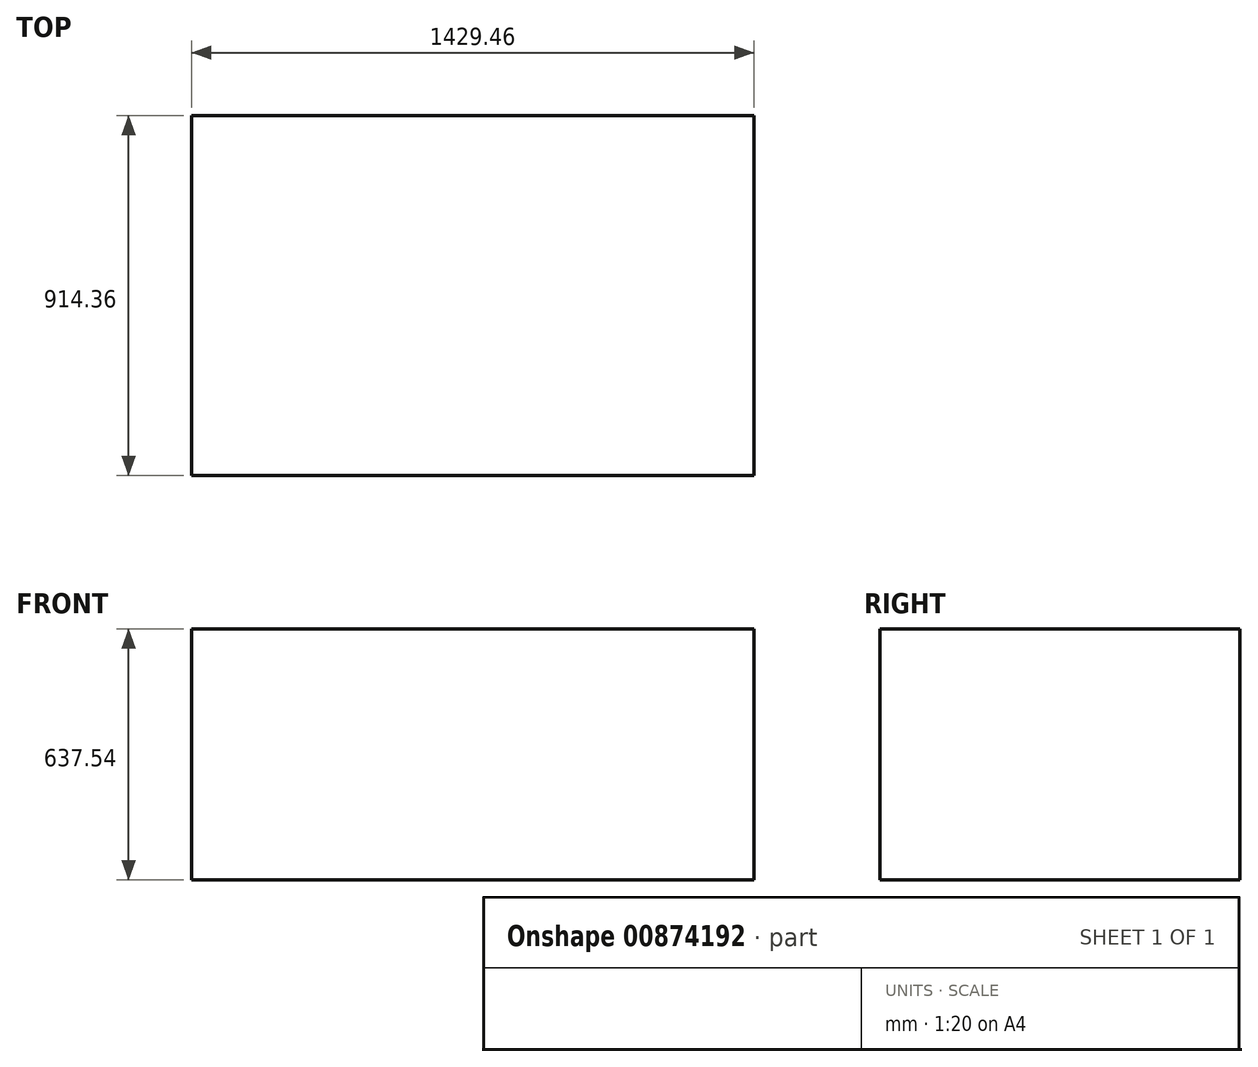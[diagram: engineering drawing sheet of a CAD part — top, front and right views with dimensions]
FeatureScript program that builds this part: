
annotation { "Feature Type Name" : "Feature", "Feature Type Description" : "" }
export const myFeature = defineFeature(function(context is Context, id is Id, definition is map)
    precondition{}
    {
        {
            var Q0;
            Q0=qCreatedBy(makeId("Top.planeOp"),FACE);
            var sketch = newSketch(context, id + "F0", { "sketchPlane" : qUnion([Q0])});
            skLineSegment(sketch, "E0.bottom", {"start": v(714.73, 457.18) * mm, "end": v(-714.73, 457.18) * mm});
            skLineSegment(sketch, "E0.top", {"start": v(714.73, -457.18) * mm, "end": v(-714.73, -457.18) * mm});
            skLineSegment(sketch, "E0.left", {"start": v(714.73, 457.18) * mm, "end": v(714.73, -457.18) * mm});
            skLineSegment(sketch, "E0.right", {"start": v(-714.73, 457.18) * mm, "end": v(-714.73, -457.18) * mm});
            skPoint(sketch, "E0.middle", {"position": v(0, 0) * mm});
            skSolve(sketch);
        }
        {
            var Q0;
            Q0=makeQuery(id+"F0.imprint","IMPRINT",FACE,{"disambiguationData":[TD([[makeQuery(id+"F0.imprint","IMPRINT",EDGE,{"derivedFrom":sQuery(id+"F0.wireOp",EDGE,"E0.bottom")}),1.0]])]});
            extrude(context, id + "F1", {"entities" : qUnion([Q0]), "depth" : 637.54 * mm, "offsetDistance" : 25.4 * mm});
        }
    });
